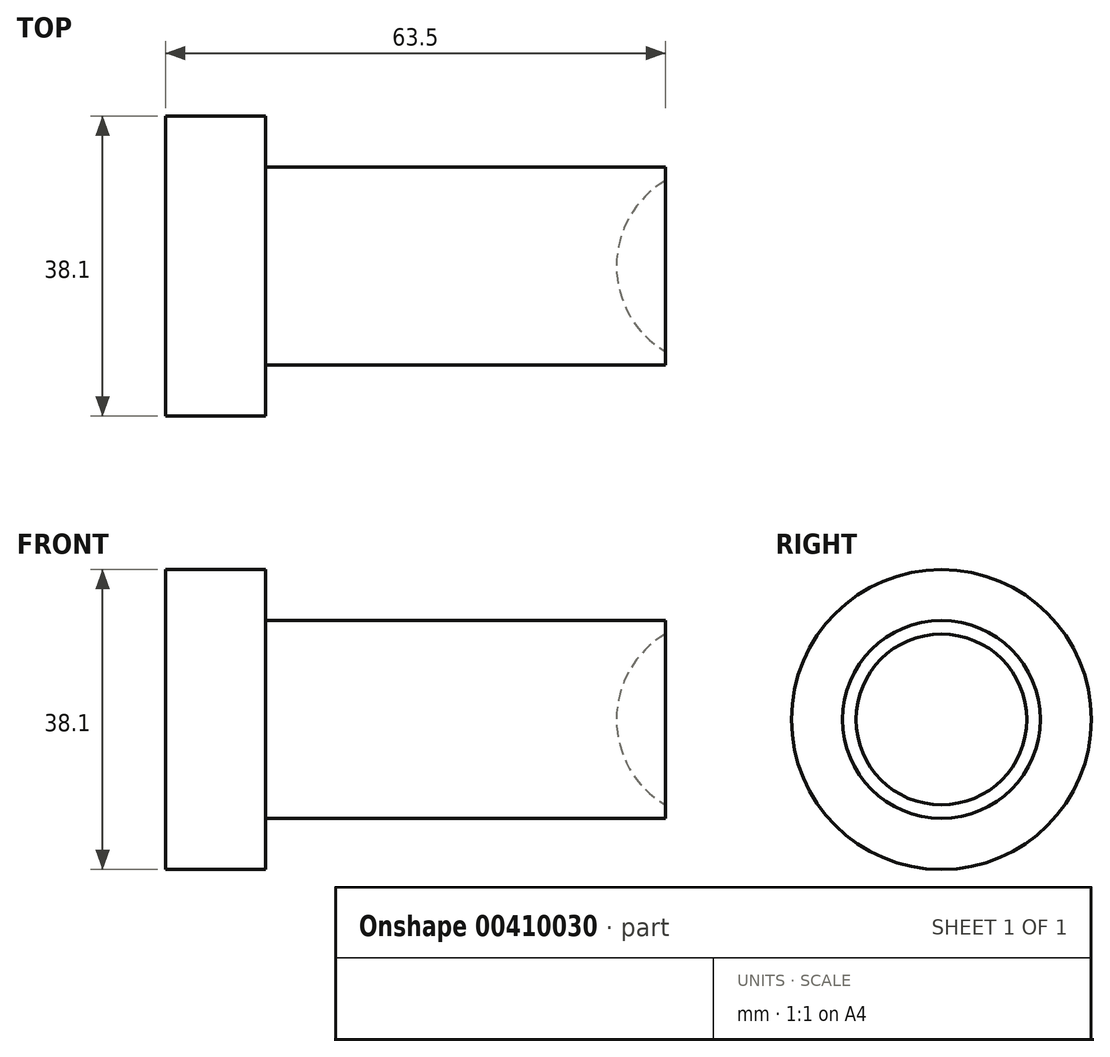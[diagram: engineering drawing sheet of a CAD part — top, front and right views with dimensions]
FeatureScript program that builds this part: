
annotation { "Feature Type Name" : "Feature", "Feature Type Description" : "" }
export const myFeature = defineFeature(function(context is Context, id is Id, definition is map)
    precondition{}
    {
        {
            var Q0;
            Q0=qCreatedBy(makeId("Front.planeOp"),FACE);
            var sketch = newSketch(context, id + "F0", { "sketchPlane" : qUnion([Q0])});
            skLineSegment(sketch, "E0.bottom", {"start": v(12.7, 12.57) * mm, "end": v(63.5, 12.57) * mm});
            skLineSegment(sketch, "E0.right", {"start": v(63.5, 12.57) * mm, "end": v(63.5, 0) * mm});
            skLineSegment(sketch, "E1.bottom", {"start": v(0, 19.05) * mm, "end": v(12.7, 19.05) * mm});
            skLineSegment(sketch, "E1.left", {"start": v(0, 19.05) * mm, "end": v(0, 0) * mm});
            skLineSegment(sketch, "E1.right", {"start": v(12.7, 19.05) * mm, "end": v(12.7, 12.57) * mm});
            skLineSegment(sketch, "E2", {"start": v(-52.44, 0) * mm, "end": v(102.69, 0) * mm, "construction": true});
            skLineSegment(sketch, "E3", {"start": v(0, 0) * mm, "end": v(63.5, 0) * mm});
            skSolve(sketch);
        }
        {
            var Q0;
            Q0 = qSketchRegion(id + "F0", true);
            var Q1;
            Q1=sQuery(id+"F0.wireOp",EDGE,"E2");
            revolve(context, id + "F1", {"entities" : qUnion([Q0]), "axis" : qUnion([Q1]), "revolveType" : RevolveType.FULL});
        }
        {
            var Q0;
            Q0=qCreatedBy(makeId("Front.planeOp"),FACE);
            var sketch = newSketch(context, id + "F2", { "sketchPlane" : qUnion([Q0])});
            skLineSegment(sketch, "E4", {"start": v(-32.54, 0) * mm, "end": v(203.98, 0) * mm, "construction": true});
            skLineSegment(sketch, "E5", {"start": v(69.85, 52.3) * mm, "end": v(69.85, -38.48) * mm, "construction": true});
            skArc(sketch, "E6", {"start": v(69.85, 12.57) * mm, "mid": v(57.28, 0) * mm, "end": v(69.85, -12.57) * mm});
            skLineSegment(sketch, "E7", {"start": v(69.85, 12.57) * mm, "end": v(69.85, -12.57) * mm});
            skSolve(sketch);
        }
        {
            var Q0;
            Q0 = qSketchRegion(id + "F2", true);
            var Q1;
            Q1=sQuery(id+"F2.wireOp",EDGE,"E5");
            revolve(context, id + "F3", {"operationType" : NewBodyOperationType.REMOVE, "entities" : qUnion([Q0]), "axis" : qUnion([Q1]), "revolveType" : RevolveType.FULL, "oppositeDirection" : true});
        }
    });
